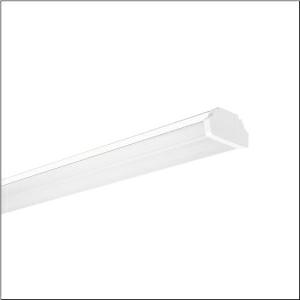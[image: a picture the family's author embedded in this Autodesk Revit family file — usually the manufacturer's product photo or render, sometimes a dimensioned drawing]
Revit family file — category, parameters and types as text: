
# Revit family: dus_r__31_mo_53bd81271v4080_fa57
name_source: partatom
category: Lighting Fixtures
units: mm (PartAtom-declared; Revit-internal decimal feet)

## family parameters
Cut with Voids When Loaded = No
Host = Face
Light Source = No
Part Type = Normal
Room Calculation Point = No
Round Connector Dimension = Use Diameter
Shared = No

## types (1)
- DUS® 31 MO (1 x LED, 7810 lm, 50.8 W, 4000K)
    Apparent Load = 51 VA
    CIE Flux Codes = 47 80 95 92 100
    Color Rendering = 80
    Color Temperature = 4000K
    Default Elevation = 1800 mm
    Description = DUS® 31 MO, luminaire insert, of sheet steel, coil coated, white, length: 1.535mm, width: 81mm, height: 90mm, 5x system unit, system units: 307mm, LED rated luminous flux: 7.810lm, light colour: 840, control gear: ON/OFF, control gear: ECG, with plug, 3-pole, with phase selection, mains connection: 220..240V, AC, 50/60Hz, rated input power: 51W, through-wiring accessed according to module size, primary optical cover: cover, of PMMA, light emission: direct distribution, primary light characteristic: symmetric, protection rating (complete): IP20, protection rating (LED compartment): IP50, insulation class (complete): insulation class I (protective earthing), certification: CE, ENEC, VDE, UKCA, impact resistance: IK03, permissible ambient temperature for indoor applications: -35..+35°C, corresponds to IFS (International Featured Standards) requirements for safety and quality in the food industry, reducing of maximum allowable ambient temperature of 5°C with ceiling mounting, packaging unit: 1 piece
    Height = 95 mm
    Lamp = 1 x LED
    Lamp Light Flux = 7810 lm
    Lamp Power = 50.8 W
    Lamp count = 1
    Length = 1535 mm
    Luminous efficacy = 154 lm/W
    Manufacturer = Siteco
    ModVariant = No
    Model = 53BD81271V4080
    Mounting Place = Ceiling
    Mounting Type = Pendant
    Number of Poles = 1
    OnlyDefault = Yes
    Power Factor = 1
    Product Name = DUS® 31 MO
    Product group = luminaire insert
    ProductGroupID = 901
    Protection Class = Protection class I
    Protection Degree = IP 20
    RLX_Detail_Level = 1
    RLX_Emergency_Light_Flux = 0 lm
    RLX_Emergency_Type = 0
    RLX_Emergency_Type_DB = No
    RlxData = <blob elided: 38441 chars, md5=7c61a51e>
    Socket = socket
    Standby Power = 0 W
    System Light Flux = 7810 lm
    System Power = 51 W
    Type Comments = Product without accessories
    Type Image = l_1313537.jpg
    URL = http://relux.com
    VarID = ---
    Voltage = 0 V
    Weight = 0.00 kg
    Width = 81 mm

## geometry (parser evidence)
native form markers: Blend x4, Sweep x13
no freeform markers — native parametric forms only
